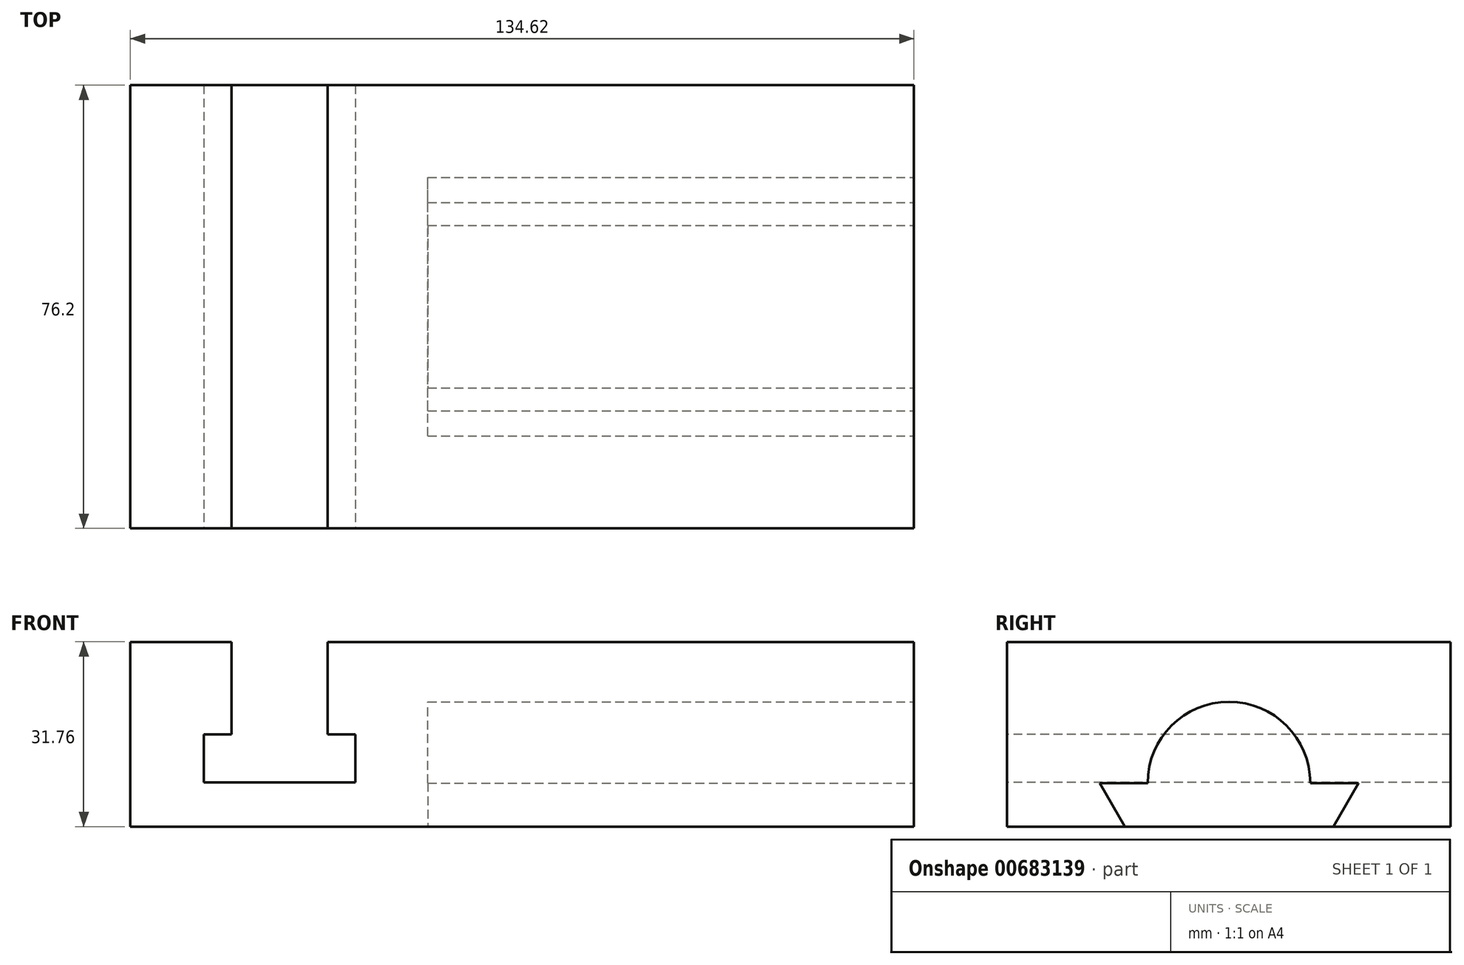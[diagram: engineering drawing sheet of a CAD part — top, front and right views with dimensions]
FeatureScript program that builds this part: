
annotation { "Feature Type Name" : "Feature", "Feature Type Description" : "" }
export const myFeature = defineFeature(function(context is Context, id is Id, definition is map)
    precondition{}
    {
        {
            var Q0;
            Q0=qCreatedBy(makeId("Top.planeOp"),FACE);
            var sketch = newSketch(context, id + "F0", { "sketchPlane" : qUnion([Q0])});
            skLineSegment(sketch, "E0.bottom", {"start": v(-67.3, -38.1) * mm, "end": v(67.31, -38.1) * mm});
            skLineSegment(sketch, "E0.top", {"start": v(-67.31, 38.1) * mm, "end": v(67.3, 38.1) * mm});
            skLineSegment(sketch, "E0.left", {"start": v(-67.3, -38.1) * mm, "end": v(-67.31, 38.1) * mm});
            skLineSegment(sketch, "E0.right", {"start": v(67.31, -38.1) * mm, "end": v(67.3, 38.1) * mm});
            skPoint(sketch, "E0.middle", {"position": v(0, 0) * mm});
            skSolve(sketch);
        }
        {
            var Q0;
            Q0 = qSketchRegion(id + "F0", true);
            extrude(context, id + "F1", {"entities" : qUnion([Q0]), "endBound" : BoundingType.SYMMETRIC, "depth" : 31.75 * mm, "offsetDistance" : 25.4 * mm});
        }
        {
            var Q0;
            Q0=makeQuery(id+"F1.opExtrude","SWEPT_FACE",FACE,{"disambiguationData":[OSD([sQuery(id+"F0.wireOp",EDGE,"E0.bottom")])]});
            var sketch = newSketch(context, id + "F2", { "sketchPlane" : qUnion([Q0])});
            skLineSegment(sketch, "E1.bottom", {"start": v(-49.91, 15.88) * mm, "end": v(-33.4, 15.88) * mm});
            skLineSegment(sketch, "E1.left", {"start": v(-49.91, 15.88) * mm, "end": v(-49.91, 0) * mm});
            skLineSegment(sketch, "E1.right", {"start": v(-33.4, 15.88) * mm, "end": v(-33.4, 0) * mm});
            skPoint(sketch, "E2", {"position": v(-41.66, 0) * mm});
            skLineSegment(sketch, "E3.bottom", {"start": v(-28.64, -8.25) * mm, "end": v(-54.67, -8.25) * mm});
            skLineSegment(sketch, "E3.left", {"start": v(-28.64, -8.25) * mm, "end": v(-28.64, 0) * mm});
            skLineSegment(sketch, "E3.right", {"start": v(-54.67, -8.25) * mm, "end": v(-54.67, 0) * mm});
            skLineSegment(sketch, "E4", {"start": v(-33.4, 0) * mm, "end": v(-28.64, 0) * mm});
            skPoint(sketch, "E5.orphan", {"position": v(-28.64, 8.26) * mm});
            skLineSegment(sketch, "E6", {"start": v(-54.67, 0) * mm, "end": v(-49.91, 0) * mm});
            skPoint(sketch, "E7.orphan", {"position": v(-54.67, 8.26) * mm});
            skSolve(sketch);
        }
        {
            var Q0;
            Q0=makeQuery(id+"F2.imprint","IMPRINT",FACE,{"disambiguationData":[TD([[makeQuery(id+"F2.imprint","IMPRINT",EDGE,{"derivedFrom":sQuery(id+"F2.wireOp",EDGE,"E1.bottom")}),-1.0]])]});
            extrude(context, id + "F3", {"entities" : qUnion([Q0]), "operationType" : NewBodyOperationType.REMOVE, "endBound" : BoundingType.THROUGH_ALL, "oppositeDirection" : true, "depth" : 76.2 * mm, "offsetDistance" : 25.4 * mm});
        }
        {
            var Q0;
            Q0=makeQuery(id+"F1.opExtrude","SWEPT_FACE",FACE,{"disambiguationData":[OSD([sQuery(id+"F0.wireOp",EDGE,"E0.right")])]});
            var sketch = newSketch(context, id + "F4", { "sketchPlane" : qUnion([Q0])});
            skPoint(sketch, "E8", {"position": v(0, 7.37) * mm});
            skPoint(sketch, "E8.positionSnap0", {"position": v(0, 7.37) * mm});
            skPoint(sketch, "E9", {"position": v(0, -15.88) * mm});
            skLineSegment(sketch, "E10", {"start": v(-17.76, -15.88) * mm, "end": v(17.93, -15.88) * mm});
            skPoint(sketch, "E11.orphan", {"position": v(-38.1, 7.37) * mm});
            skPoint(sketch, "E12.end.orphan", {"position": v(38.1, 7.37) * mm});
            skPoint(sketch, "E13.orphan", {"position": v(-38.1, -8.5) * mm});
            skLineSegment(sketch, "E14", {"start": v(-22.2, -8.4) * mm, "end": v(-17.89, -15.88) * mm});
            skLineSegment(sketch, "E15", {"start": v(17.93, -15.88) * mm, "end": v(22.25, -8.4) * mm});
            skPoint(sketch, "E16.centerSnap0", {"position": v(0.02, -8.4) * mm});
            skArc(sketch, "E17", {"start": v(14, -8.4) * mm, "mid": v(0.02, 5.57) * mm, "end": v(-13.95, -8.4) * mm});
            skLineSegment(sketch, "E18", {"start": v(-22.2, -8.4) * mm, "end": v(22.25, -8.4) * mm});
            skSolve(sketch);
        }
        {
            var Q0;
            {var subQ0=sQuery(id+"F4.wireOp",EDGE,"E17");Q0=makeQuery(id+"F4.imprint","IMPRINT",FACE,{"disambiguationData":[TD([[makeQuery(id+"F4.imprint","IMPRINT",EDGE,{"derivedFrom":subQ0}),1.0]])]});}
            var Q1;
            {var subQ5=sQuery(id+"F4.wireOp",EDGE,"E14");Q1=makeQuery(id+"F4.imprint","IMPRINT",FACE,{"disambiguationData":[TD([[makeQuery(id+"F4.imprint","IMPRINT",EDGE,{"derivedFrom":subQ5}),1.0]])]});}
            extrude(context, id + "F5", {"entities" : qUnion([Q0, Q1]), "operationType" : NewBodyOperationType.REMOVE, "oppositeDirection" : true, "depth" : 83.52 * mm, "offsetDistance" : 25.4 * mm});
        }
        {
            var Q0;
            Q0=makeQuery(id+"F1.opExtrude","SWEPT_BODY",BODY,{"disambiguationData":[OSD([sQuery(id+"F0.wireOp",EDGE,"E0.bottom"),sQuery(id+"F0.wireOp",EDGE,"E0.top"),sQuery(id+"F0.wireOp",EDGE,"E0.left"),sQuery(id+"F0.wireOp",EDGE,"E0.right")])]});
            transform(context, id + "F6", {"entities" : qUnion([Q0]), "transformType" : TransformType.TRANSLATION_3D, "dx" : 0 * mm, "dy" : 0 * mm, "dz" : 0 * mm, "makeCopy" : true});
        }
        {
            var Q0;
            Q0=makeQuery(id+"F6.opPattern","COPY",BODY,{"derivedFrom":makeQuery(id+"F1.opExtrude","SWEPT_BODY",BODY,{"disambiguationData":[OSD([sQuery(id+"F0.wireOp",EDGE,"E0.bottom"),sQuery(id+"F0.wireOp",EDGE,"E0.top"),sQuery(id+"F0.wireOp",EDGE,"E0.left"),sQuery(id+"F0.wireOp",EDGE,"E0.right")])]}),"instanceName":"1"});
            deleteBodies(context, id + "F7", {"entities" : qUnion([Q0])});
        }
    });
